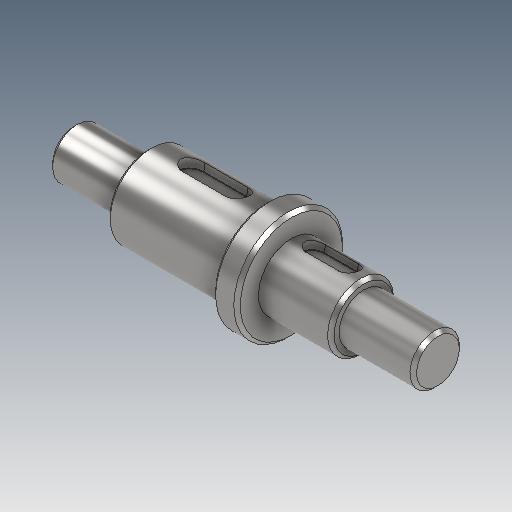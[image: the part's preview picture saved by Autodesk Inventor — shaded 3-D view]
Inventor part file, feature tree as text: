
AUTODESK INVENTOR PART (.ipt)
format: ipt  version: 2025 (Build 290162000, 162)  size: 280,064 bytes
history: native  units: mm
features: other x7, chamfer x6, revolve x1
ambient origin geometry x6: Origin, XZ Plane, XY Plane, X Axis, Y Axis, Z Axis
bodies: 实体1 (feature_tree)
feature tree (14):
  other  "{BB8FE430-83BF-418D-8DF9-9B323D3DB9B9}"
  revolve  "旋转1"  [1 undecoded]
  chamfer  "倒角6"  Distance=30.0mm
  chamfer  "倒角7"  Distance=50.0mm
  chamfer  "倒角1"  Distance=66.0mm
  chamfer  "倒角2"  Distance=40.0mm
  chamfer  "倒角3"  Distance=30.0mm
  chamfer  "倒角5"  [1 undecoded]
  other  "键槽3"
  other  "键槽4"
  other  "起始平面"
  other  "主草图"
  other  "轴键槽"
  other  "轴键槽2"
note: 2 required parameter values undecoded (feature->parameter linkage not recoverable at this tier; creation-order binding heuristic only, values carry confidence <= 0.55)